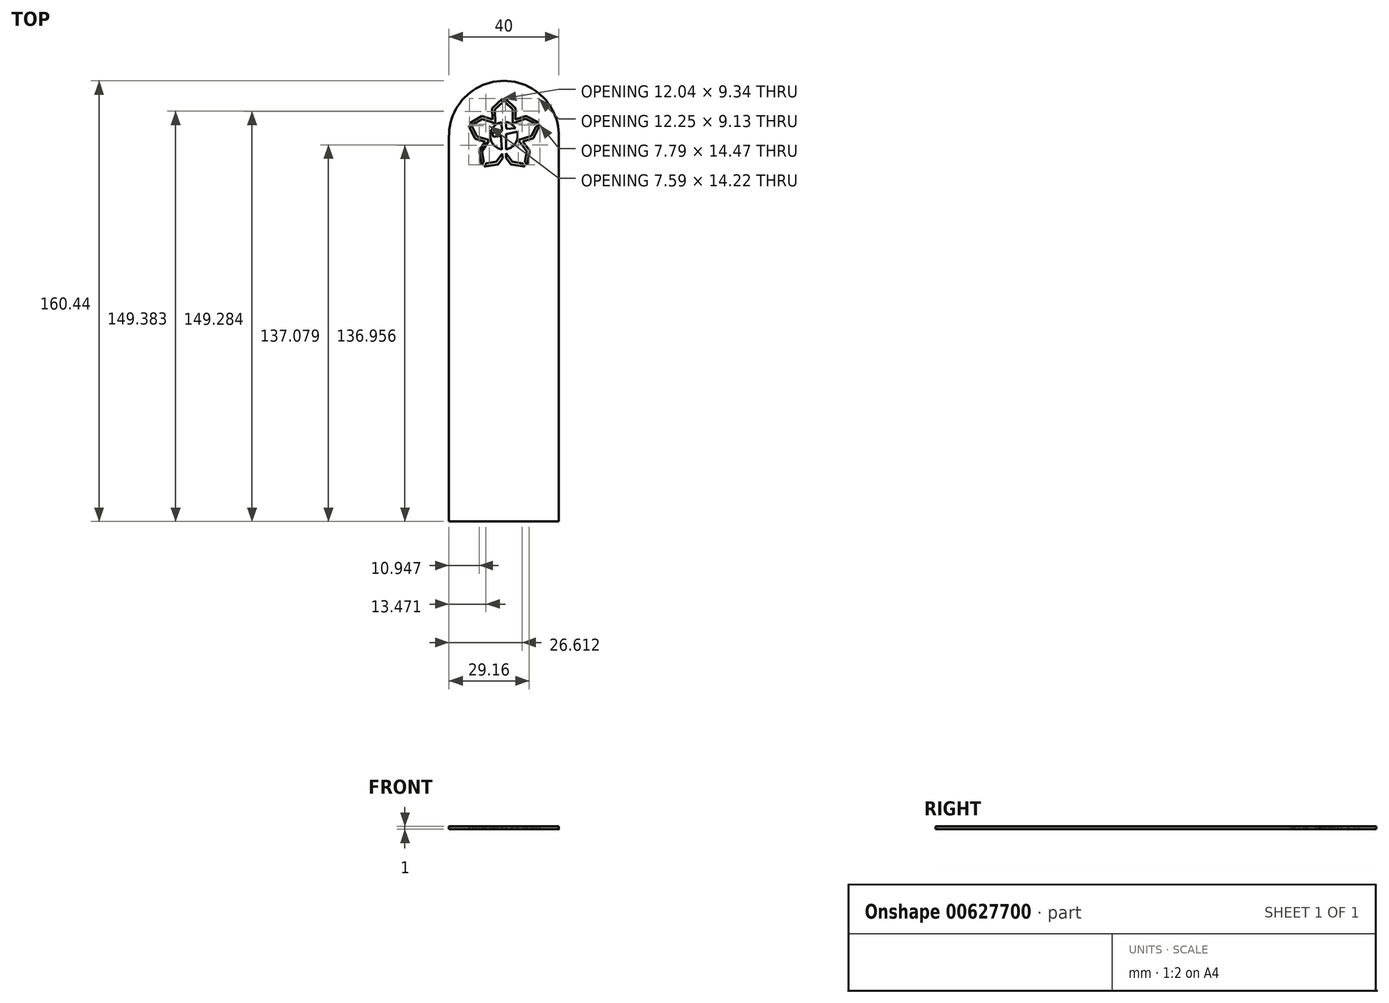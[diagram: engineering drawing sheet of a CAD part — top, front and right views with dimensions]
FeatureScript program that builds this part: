
annotation { "Feature Type Name" : "Feature", "Feature Type Description" : "" }
export const myFeature = defineFeature(function(context is Context, id is Id, definition is map)
    precondition{}
    {
        {
            var Q0;
            Q0=qCreatedBy(makeId("Top.planeOp"),FACE);
            var sketch = newSketch(context, id + "F0", { "sketchPlane" : qUnion([Q0])});
            skLineSegment(sketch, "E0", {"start": v(-29.48, 59.06) * mm, "end": v(-34.17, 60.58) * mm});
            skLineSegment(sketch, "E1", {"start": v(-34.17, 60.58) * mm, "end": v(-37.52, 58.7) * mm});
            skLineSegment(sketch, "E2", {"start": v(-37.82, 57.75) * mm, "end": v(-36.1, 54.29) * mm});
            skLineSegment(sketch, "E3", {"start": v(-36.1, 54.29) * mm, "end": v(-31.55, 52.93) * mm});
            skLineSegment(sketch, "E4", {"start": v(-31.55, 52.93) * mm, "end": v(-34.28, 48.84) * mm});
            skLineSegment(sketch, "E5", {"start": v(-34.28, 48.84) * mm, "end": v(-33.58, 45.07) * mm});
            skLineSegment(sketch, "E6", {"start": v(-32.76, 44.49) * mm, "end": v(-29.04, 45.05) * mm});
            skLineSegment(sketch, "E7", {"start": v(-29.04, 45.05) * mm, "end": v(-26.95, 47.96) * mm});
            skLineSegment(sketch, "E8", {"start": v(-25.5, 48.12) * mm, "end": v(-23.23, 45.05) * mm});
            skLineSegment(sketch, "E9", {"start": v(-23.23, 45.05) * mm, "end": v(-19.49, 44.49) * mm});
            skLineSegment(sketch, "E10", {"start": v(-18.67, 45.07) * mm, "end": v(-17.96, 48.84) * mm});
            skLineSegment(sketch, "E11", {"start": v(-17.96, 48.84) * mm, "end": v(-21.03, 52.93) * mm});
            skLineSegment(sketch, "E12", {"start": v(-21.03, 52.93) * mm, "end": v(-16.27, 54.48) * mm});
            skLineSegment(sketch, "E13", {"start": v(-16.27, 54.48) * mm, "end": v(-14.56, 57.96) * mm});
            skLineSegment(sketch, "E14", {"start": v(-14.88, 58.9) * mm, "end": v(-18.36, 60.69) * mm});
            skLineSegment(sketch, "E15", {"start": v(-18.36, 60.69) * mm, "end": v(-23.1, 59.01) * mm});
            skLineSegment(sketch, "E16", {"start": v(-23.1, 59.01) * mm, "end": v(-23.1, 64.1) * mm});
            skLineSegment(sketch, "E17", {"start": v(-23.1, 64.1) * mm, "end": v(-25.8, 66.67) * mm});
            skLineSegment(sketch, "E18", {"start": v(-26.8, 66.67) * mm, "end": v(-29.59, 64.1) * mm});
            skLineSegment(sketch, "E19", {"start": v(-29.59, 64.1) * mm, "end": v(-29.48, 59.06) * mm});
            skLineSegment(sketch, "E20", {"start": v(-25.39, 56.97) * mm, "end": v(-22.09, 57.24) * mm});
            skLineSegment(sketch, "E21", {"start": v(-25.5, 55.17) * mm, "end": v(-25.5, 49.6) * mm});
            skLineSegment(sketch, "E22", {"start": v(-26.85, 46.39) * mm, "end": v(-26.95, 47.96) * mm});
            skLineSegment(sketch, "E23", {"start": v(-27.36, 54.62) * mm, "end": v(-30.05, 54.08) * mm});
            skLineSegment(sketch, "E24", {"start": v(-30.05, 54.08) * mm, "end": v(-30.74, 55.5) * mm});
            skLineSegment(sketch, "E25", {"start": v(-30.74, 55.5) * mm, "end": v(-27.06, 56.25) * mm});
            skLineSegment(sketch, "E26", {"start": v(-27.06, 56.25) * mm, "end": v(-27.13, 59.46) * mm});
            skArc(sketch, "E27", {"start": v(-6.3, 54.09) * mm, "mid": v(-26.29, 74.53) * mm, "end": v(-46.28, 54.09) * mm});
            skLineSegment(sketch, "E28", {"start": v(-46.28, 54.09) * mm, "end": v(-46.28, -85.91) * mm});
            skLineSegment(sketch, "E29", {"start": v(-6.3, 54.09) * mm, "end": v(-6.3, -85.91) * mm});
            skLineSegment(sketch, "E30", {"start": v(-46.28, -85.91) * mm, "end": v(-6.3, -85.91) * mm});
            skLineSegment(sketch, "E31", {"start": v(-35.33, 49.06) * mm, "end": v(-33.13, 52.36) * mm});
            skLineSegment(sketch, "E32", {"start": v(-35.33, 49.06) * mm, "end": v(-34.39, 43.93) * mm});
            skLineSegment(sketch, "E33", {"start": v(-33.57, 43.35) * mm, "end": v(-28.47, 44.13) * mm});
            skLineSegment(sketch, "E34", {"start": v(-28.47, 44.13) * mm, "end": v(-26.85, 46.39) * mm});
            skLineSegment(sketch, "E35", {"start": v(-25.5, 46.44) * mm, "end": v(-23.79, 44.13) * mm});
            skLineSegment(sketch, "E36", {"start": v(-23.79, 44.13) * mm, "end": v(-18.68, 43.36) * mm});
            skLineSegment(sketch, "E37", {"start": v(-16.9, 49.09) * mm, "end": v(-17.87, 43.93) * mm});
            skLineSegment(sketch, "E38", {"start": v(-19.39, 52.41) * mm, "end": v(-16.9, 49.09) * mm});
            skLineSegment(sketch, "E39", {"start": v(-19.39, 52.41) * mm, "end": v(-15.56, 53.66) * mm});
            skLineSegment(sketch, "E40", {"start": v(-13.23, 58.4) * mm, "end": v(-15.56, 53.66) * mm});
            skLineSegment(sketch, "E41", {"start": v(-18.3, 61.77) * mm, "end": v(-13.55, 59.35) * mm});
            skLineSegment(sketch, "E42", {"start": v(-22.1, 60.43) * mm, "end": v(-18.3, 61.77) * mm});
            skLineSegment(sketch, "E43", {"start": v(-30.6, 64.53) * mm, "end": v(-26.8, 68.04) * mm});
            skLineSegment(sketch, "E44", {"start": v(-30.6, 64.53) * mm, "end": v(-30.5, 60.44) * mm});
            skLineSegment(sketch, "E45", {"start": v(-25.8, 68.04) * mm, "end": v(-22.1, 64.53) * mm});
            skLineSegment(sketch, "E46", {"start": v(-34.28, 61.66) * mm, "end": v(-30.5, 60.44) * mm});
            skLineSegment(sketch, "E47", {"start": v(-38.84, 59.11) * mm, "end": v(-34.28, 61.66) * mm});
            skLineSegment(sketch, "E48", {"start": v(-39.14, 58.16) * mm, "end": v(-36.8, 53.45) * mm});
            skLineSegment(sketch, "E49", {"start": v(-36.8, 53.45) * mm, "end": v(-33.13, 52.36) * mm});
            skLineSegment(sketch, "E50", {"start": v(-38.84, 59.11) * mm, "end": v(-37.52, 58.7) * mm});
            skLineSegment(sketch, "E51", {"start": v(-39.14, 58.16) * mm, "end": v(-37.82, 57.75) * mm});
            skLineSegment(sketch, "E52", {"start": v(-33.57, 43.35) * mm, "end": v(-32.76, 44.49) * mm});
            skLineSegment(sketch, "E53", {"start": v(-34.39, 43.93) * mm, "end": v(-33.58, 45.07) * mm});
            skLineSegment(sketch, "E54", {"start": v(-18.68, 43.36) * mm, "end": v(-19.49, 44.49) * mm});
            skLineSegment(sketch, "E55", {"start": v(-18.67, 45.07) * mm, "end": v(-17.87, 43.93) * mm});
            skLineSegment(sketch, "E56", {"start": v(-25.8, 68.04) * mm, "end": v(-25.8, 66.67) * mm});
            skLineSegment(sketch, "E57", {"start": v(-26.8, 68.04) * mm, "end": v(-26.8, 66.67) * mm});
            skLineSegment(sketch, "E58", {"start": v(-14.88, 58.9) * mm, "end": v(-13.55, 59.35) * mm});
            skLineSegment(sketch, "E59", {"start": v(-14.56, 57.96) * mm, "end": v(-13.23, 58.4) * mm});
            skLineSegment(sketch, "E60.trimOffspring", {"start": v(-22.1, 60.43) * mm, "end": v(-22.1, 64.53) * mm});
            skArc(sketch, "E61", {"start": v(-25.5, 49.6) * mm, "mid": v(-22.05, 51.88) * mm, "end": v(-21.5, 55.98) * mm});
            skLineSegment(sketch, "E62.trimOffspring", {"start": v(-27.05, 49.59) * mm, "end": v(-27.36, 54.62) * mm});
            skLineSegment(sketch, "E63.trimOffspring", {"start": v(-25.5, 48.12) * mm, "end": v(-25.5, 46.44) * mm});
            skArc(sketch, "E64.trimOffspring", {"start": v(-22.09, 57.24) * mm, "mid": v(-23.6, 58.75) * mm, "end": v(-25.6, 59.48) * mm});
            skLineSegment(sketch, "E65.trimOffspring", {"start": v(-21.5, 55.98) * mm, "end": v(-25.5, 55.17) * mm});
            skArc(sketch, "E66.trimOffspring", {"start": v(-27.13, 59.46) * mm, "mid": v(-31.29, 54.49) * mm, "end": v(-27.05, 49.59) * mm});
            skLineSegment(sketch, "E67.trimOffspring", {"start": v(-25.6, 59.48) * mm, "end": v(-25.39, 56.97) * mm});
            skSolve(sketch);
        }
        {
            var Q0;
            Q0=makeQuery(id+"F0.imprint","IMPRINT",FACE,{"disambiguationData":[TD([[makeQuery(id+"F0.imprint","IMPRINT",EDGE,{"derivedFrom":sQuery(id+"F0.wireOp",EDGE,"E0")}),1.0]])]});
            extrude(context, id + "F1", {"entities" : qUnion([Q0]), "depth" : 1 * mm, "offsetDistance" : 25 * mm});
        }
    });
